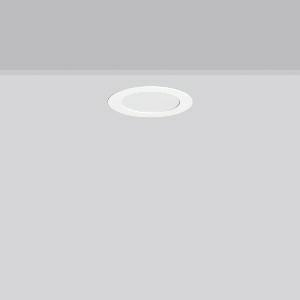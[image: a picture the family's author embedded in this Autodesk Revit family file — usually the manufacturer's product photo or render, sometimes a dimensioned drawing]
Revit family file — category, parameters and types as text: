
# Revit family: toledo_flat__round_e_901807_002_2_76_08c6
name_source: partatom
category: Lighting Fixtures
units: mm (PartAtom-declared; Revit-internal decimal feet)

## family parameters
Cut with Voids When Loaded = No
Host = Face
Light Source = No
Part Type = Normal
Room Calculation Point = No
Round Connector Dimension = Use Diameter
Shared = No

## types (1)
- TuneableWhite 827 (1 x LED Modul 827, 860 lm, 2700)
    Apparent Load = 10 VA
    CIE Flux Codes = 47 79 96 100 100
    Color Rendering = 80
    Color Temperature = 2700
    Default Elevation = 1800 mm
    Description = Series: TOLEDO FLAT+ round
Flexible round recessed multifunction downlight. Housing: sheet steel, powder-coated. Luminaire frame: aluminium, powder-coated. Light guide and diffuser made of non-yellowing PMMA, opal matt. LED backlight technology for homogeneous illumination of the entire light-emitting surface. Tunable white dynamically adjustable from 2700 K to 6500 K. Suitable for Recessed ceiling mounting. Ceiling installation with spring system. Can be directly covered with thermal insulation material (applies only to the lower lumen levels). Including separate LED converter with connecting cable 250 mm. Surface mounted housing as accessory for all sizes. 
Colour: white
Diameter: 165 mm
Height: 2 mm
Cut-out diameter: 152 mm
Recess height: 90 mm
Luminaire: recess height: 35 mm
Lamp: LED
Socket: without socket
Colour temperature: 2700K - 6500K
Colour rendering index (CRI): 80
System power: 10 W
Rated luminous flux: 860 lm
Luminous efficiency: 86 lm/W
System power 2: 10 W
Rated luminous flux 2: 890 lm
Luminous efficiency 2: 89 lm/W
System power 3: 10 W
Rated luminous flux 3: 890 lm
Luminous efficiency 3: 89 lm/W
Control gear: Converter, dimmable, DALI
Protection class: II
Type of protection: IP 54
    Height = 0 mm  [stored 0 ft]
    Lamp = 1 x LED Modul 827
    Lamp Light Flux = 860 lm
    Lamp count = 1
    Length = 165 mm
    Lifetime = 50000 h
    Luminous efficacy = 86 lm/W
    Manufacturer = RZB
    ModVariant = No
    Model = 901807.002.2.76
    Mounting Place = Ceiling
    Mounting Type = Recessed
    Number of Poles = 1
    OnlyDefault = Yes
    Power Factor = 1
    Product Name = TOLEDO FLAT+ round E
    Product group = Recessed downlights
    ProductGroupID = 402
    Protection Class = Protection class II
    Protection Degree = Degree of protection
    RLX_Detail_Level = 1
    RLX_Emergency_Light_Flux = 0 lm
    RLX_Emergency_Type = 0
    RLX_Emergency_Type_DB = No
    RlxData = <blob elided: 27089 chars, md5=b70dd158>
    Socket = socket
    Standby Power = 0 W
    System Light Flux = 860 lm
    System Power = 10 W
    Type Comments = TuneableWhite 827
    Type Image = 901807.002.jpg
    URL = http://relux.com
    VarID = tuneablewhite_827
    Voltage = 0 V
    Weight = 0.00 kg
    Width = 0 mm  [stored 0 ft]

note: [stored X ft] marks values corroborated as IEEE doubles in the binary element streams (Revit-internal decimal feet)

## geometry (parser evidence)
native form markers: Blend x4, Sweep x9
no freeform markers — native parametric forms only
